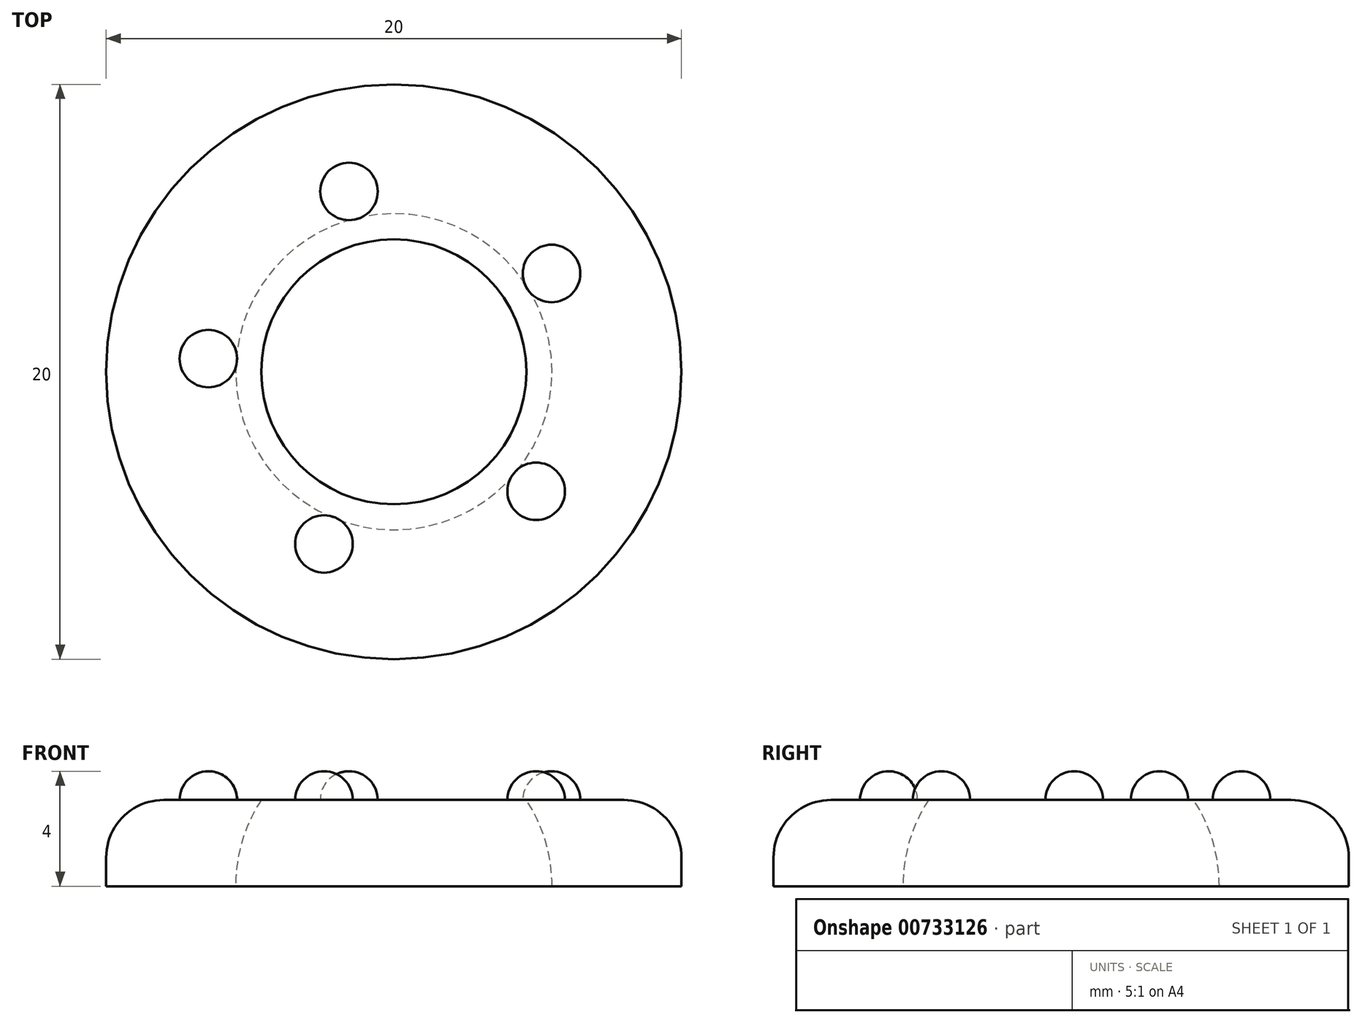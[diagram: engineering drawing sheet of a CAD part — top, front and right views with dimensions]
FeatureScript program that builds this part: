
annotation { "Feature Type Name" : "Feature", "Feature Type Description" : "" }
export const myFeature = defineFeature(function(context is Context, id is Id, definition is map)
    precondition{}
    {
        {
            var Q0;
            Q0=qCreatedBy(makeId("Front.planeOp"),FACE);
            var sketch = newSketch(context, id + "F0", { "sketchPlane" : qUnion([Q0])});
            skLineSegment(sketch, "E0", {"start": v(0, 0) * mm, "end": v(0, 3.52) * mm});
            skCircle(sketch, "E1", {"center": v(0, 0) * mm, "radius": 5 * mm});
            skArc(sketch, "E2.0", {"start": v(-4.6, 3) * mm, "mid": v(-5.27, 1.56) * mm, "end": v(-5.5, 0) * mm});
            skLineSegment(sketch, "E3", {"start": v(0, 0) * mm, "end": v(-5, 0) * mm});
            skLineSegment(sketch, "E4", {"start": v(-10, 0) * mm, "end": v(-10, 3) * mm});
            skLineSegment(sketch, "E5", {"start": v(-10, 3) * mm, "end": v(-4.6, 3) * mm});
            skPoint(sketch, "E6.start.orphan", {"position": v(-5, 0) * mm});
            skLineSegment(sketch, "E7.trimOffspring", {"start": v(-5.5, 0) * mm, "end": v(-10, 0) * mm});
            skSolve(sketch);
        }
        {
            var Q0;
            Q0=makeQuery(id+"F0.imprint","IMPRINT",FACE,{"disambiguationData":[TD([[makeQuery(id+"F0.imprint","IMPRINT",EDGE,{"derivedFrom":sQuery(id+"F0.wireOp",EDGE,"E2.0")}),-1.0]])]});
            var Q1;
            Q1=sQuery(id+"F0.wireOp",EDGE,"E0");
            revolve(context, id + "F1", {"surfaceOperationType" : NewSurfaceOperationType.NEW, "entities" : qUnion([Q0]), "axis" : qUnion([Q1]), "revolveType" : RevolveType.FULL});
        }
        {
            var Q0;
            Q0=makeQuery(id+"F1.opRevolve","SWEPT_EDGE",EDGE,{"disambiguationData":[OSD([sQuery(id+"F0.wireOp",EDGE,"E4"),sQuery(id+"F0.wireOp",EDGE,"E5")])]});
            fillet(context, id + "F2", {"entities" : qUnion([Q0]), "radius" : 2 * mm, "tangentPropagation" : true, "allowEdgeOverflow" : false});
        }
        {
            var Q0;
            Q0=makeQuery(id+"F1.opRevolve","SWEPT_FACE",FACE,{"disambiguationData":[OSD([sQuery(id+"F0.wireOp",EDGE,"E5")])]});
            var sketch = newSketch(context, id + "F3", { "sketchPlane" : qUnion([Q0])});
            skCircle(sketch, "E8", {"center": v(-6.45, 0.46) * mm, "radius": 1 * mm});
            skSolve(sketch);
        }
        {
            var Q0;
            Q0=makeQuery(id+"F3.imprint","IMPRINT",FACE,{"disambiguationData":[TD([[makeQuery(id+"F3.imprint","IMPRINT",EDGE,{"derivedFrom":sQuery(id+"F3.wireOp",EDGE,"E8")}),1.0]])]});
            extrude(context, id + "F4", {"entities" : qUnion([Q0]), "depth" : 1 * mm, "offsetDistance" : 25 * mm});
        }
        {
            var Q0;
            Q0=makeQuery(id+"F4.opExtrude","CAP_FACE",FACE,{"disambiguationData":[OSD([sQuery(id+"F3.wireOp",EDGE,"E8")])],"isStart":false});
            fillet(context, id + "F5", {"entities" : qUnion([Q0]), "radius" : 1 * mm, "tangentPropagation" : true, "allowEdgeOverflow" : false});
        }
        {
            var Q0;
            Q0=makeQuery(id+"F4.opExtrude","SWEPT_BODY",BODY,{"disambiguationData":[OSD([sQuery(id+"F3.wireOp",EDGE,"E8")])]});
            var Q1;
            Q1=makeQuery(id+"F1.opRevolve","SWEPT_EDGE",EDGE,{"disambiguationData":[OSD([sQuery(id+"F0.wireOp",EDGE,"E2.0"),sQuery(id+"F0.wireOp",EDGE,"E5")])]});
            circularPattern(context, id + "F6", {"entities" : qUnion([Q0]), "axis" : qUnion([Q1]), "angle" : 360 * degree, "instanceCount" : 5, "equalSpace" : true});
        }
    });
